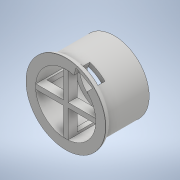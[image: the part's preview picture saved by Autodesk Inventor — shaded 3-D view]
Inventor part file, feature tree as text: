
AUTODESK INVENTOR PART (.ipt)
format: ipt  version: 2021 (Build 250183000, 183)  size: 346,624 bytes
history: native  units: mm
features: extrude x11, sketch x11, other x1, fillet x1
ambient origin geometry x8: Origin, YZ Plane, XZ Plane, XY Plane, X Axis, Y Axis, Z Axis, Center Point
bodies: Body1 (feature_tree), Body2 (feature_tree), Body3 (feature_tree)
feature tree (24):
  other  "Sólido1"
  extrude  "Extrusión1"  Depth=144.0mm
  extrude  "Extrusión2"  Depth=100.0mm TaperAngle=0.0deg
  extrude  "Extrusión3"  Depth=124.0mm
  extrude  "Extrusión4"  Depth=95.0mm
  fillet  "Empalme1"  Radius=124.0mm
  extrude  "Extrusión5"  Depth=80.0mm
  extrude  "Extrusión6"  Depth=15.0mm TaperAngle=0.0deg
  extrude  "Extrusión7"  Depth=15.0mm
  extrude  "Extrusión8"  Depth=10.0mm TaperAngle=0.0deg
  extrude  "Extrusión9"  Depth=17.5mm TaperAngle=0.0deg
  extrude  "Extrusión10"  Depth=67.25mm TaperAngle=0.0deg
  extrude  "Extrusión11"  [1 undecoded]
  sketch  "Boceto1"  dims[d5=124.0mm d6=144.0mm]
  sketch  "Boceto5"  dims[d7=104.0mm d8=100.0mm d9=0.0mm]
  sketch  "Boceto6"  dims[d11=104.0mm d12=124.0mm]
  sketch  "Boceto7"  dims[d13=95.0mm d14=0.0mm d15=104.0mm d16=124.0mm]
  sketch  "Boceto8"  dims[d17=80.0mm d18=0.0mm d19=164.0mm]
  sketch  "Boceto9"  dims[d20=144.0mm d21=15.0mm d22=0.0mm]
  sketch  "Boceto10"  dims[d23=15.0mm d25=124.0mm]
  sketch  "Boceto11"  dims[d26=30.0mm d27=0.0mm d30=10.0mm d31=0.0mm]
  sketch  "Boceto14"  dims[d32=8.0mm d33=0.0mm d34=17.5mm d35=0.0mm]
  sketch  "Boceto15"  dims[d36=10.0mm d37=0.0mm d38=67.25mm d39=0.0mm]
  sketch  "Boceto16"  dims[d40=64.5mm d41=0.0mm]
note: 1 required parameter value undecoded (feature->parameter linkage not recoverable at this tier; creation-order binding heuristic only, values carry confidence <= 0.55)
